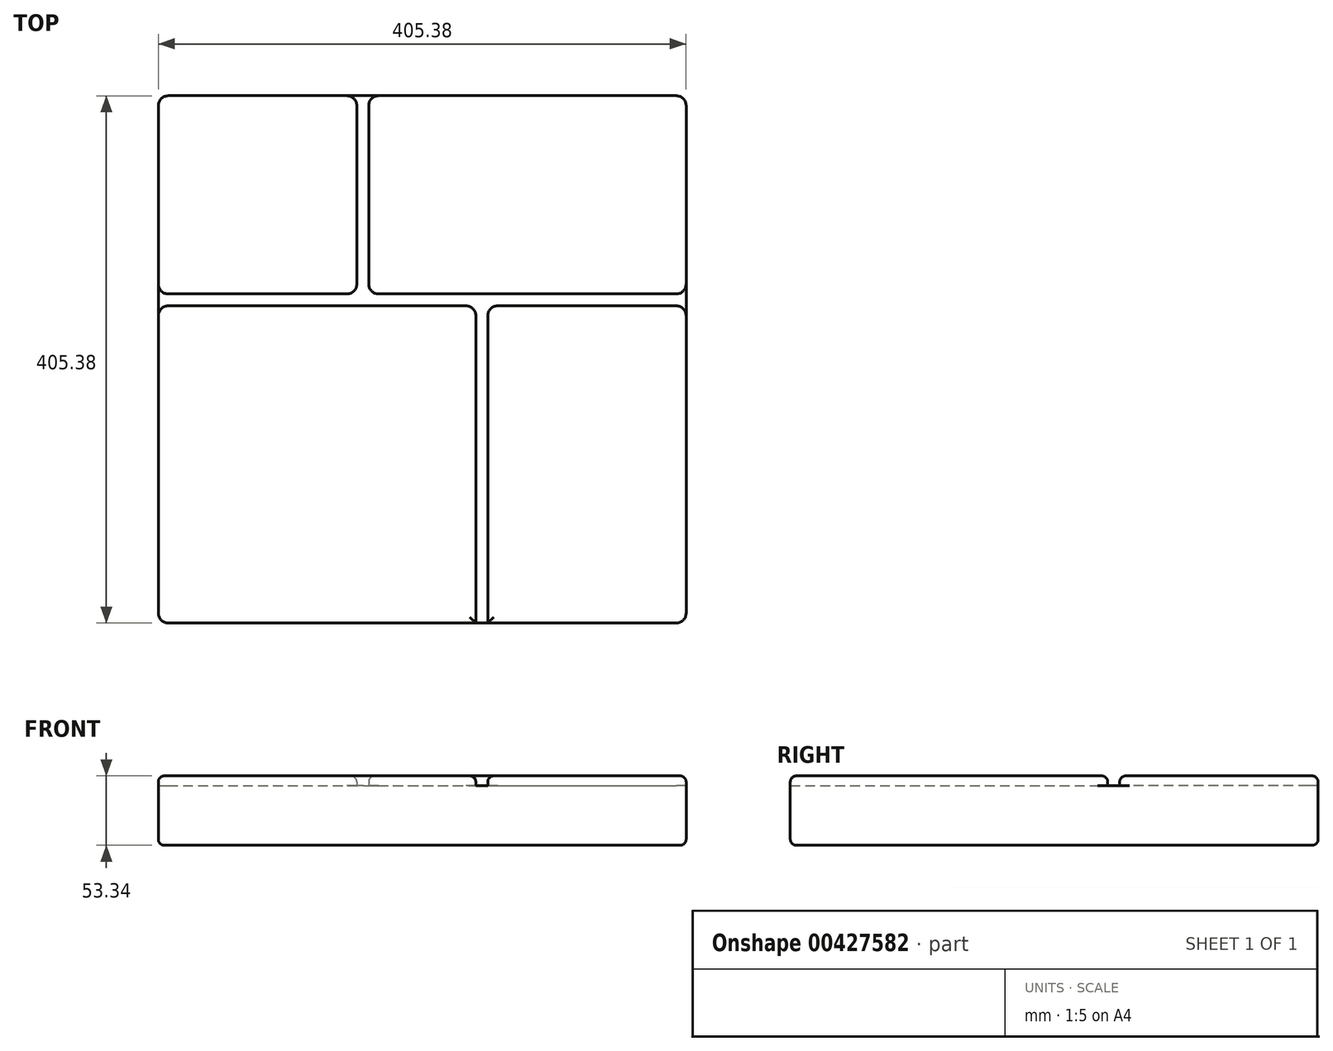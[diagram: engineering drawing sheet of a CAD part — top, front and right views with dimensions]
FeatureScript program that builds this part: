
annotation { "Feature Type Name" : "Feature", "Feature Type Description" : "" }
export const myFeature = defineFeature(function(context is Context, id is Id, definition is map)
    precondition{}
    {
        {
            var Q0;
            Q0=qCreatedBy(makeId("Top.planeOp"),FACE);
            var sketch = newSketch(context, id + "F0", { "sketchPlane" : qUnion([Q0])});
            skLineSegment(sketch, "E0.bottom", {"start": v(202.7, -202.7) * mm, "end": v(-202.7, -202.7) * mm});
            skLineSegment(sketch, "E0.top", {"start": v(202.7, 202.7) * mm, "end": v(-202.7, 202.7) * mm});
            skLineSegment(sketch, "E0.left", {"start": v(202.7, -202.7) * mm, "end": v(202.7, 202.7) * mm});
            skLineSegment(sketch, "E0.right", {"start": v(-202.7, -202.7) * mm, "end": v(-202.7, 202.7) * mm});
            skPoint(sketch, "E0.middle", {"position": v(0, 0) * mm});
            skSolve(sketch);
        }
        {
            var Q0;
            Q0=makeQuery(id+"F0.imprint","IMPRINT",FACE,{"disambiguationData":[TD([[makeQuery(id+"F0.imprint","IMPRINT",EDGE,{"derivedFrom":sQuery(id+"F0.wireOp",EDGE,"E0.bottom")}),-1.0]])]});
            extrude(context, id + "F1", {"entities" : qUnion([Q0]), "depth" : 45.72 * mm});
        }
        {
            var Q0;
            Q0=makeQuery(id+"F1.opExtrude","CAP_FACE",FACE,{"disambiguationData":[OSD([sQuery(id+"F0.wireOp",EDGE,"E0.bottom"),sQuery(id+"F0.wireOp",EDGE,"E0.top"),sQuery(id+"F0.wireOp",EDGE,"E0.left"),sQuery(id+"F0.wireOp",EDGE,"E0.right")])],"isStart":false});
            var sketch = newSketch(context, id + "F2", { "sketchPlane" : qUnion([Q0])});
            skLineSegment(sketch, "E1.bottom", {"start": v(-202.7, -202.7) * mm, "end": v(41.15, -202.7) * mm});
            skLineSegment(sketch, "E1.left", {"start": v(-202.7, -202.7) * mm, "end": v(-202.7, 33.53) * mm});
            skLineSegment(sketch, "E1.right", {"start": v(41.15, -202.7) * mm, "end": v(41.15, 33.53) * mm});
            skLineSegment(sketch, "E2.bottom", {"start": v(-202.7, 202.7) * mm, "end": v(-57.91, 202.7) * mm});
            skLineSegment(sketch, "E2.top", {"start": v(-195.07, 50.3) * mm, "end": v(-57.91, 50.3) * mm});
            skLineSegment(sketch, "E2.left", {"start": v(-202.7, 202.7) * mm, "end": v(-202.7, 57.91) * mm});
            skLineSegment(sketch, "E2.right", {"start": v(-50.3, 195.07) * mm, "end": v(-50.3, 57.91) * mm});
            skLineSegment(sketch, "E3.bottom", {"start": v(-33.53, 202.7) * mm, "end": v(202.7, 202.7) * mm});
            skLineSegment(sketch, "E3.top", {"start": v(-33.53, 50.3) * mm, "end": v(195.07, 50.3) * mm});
            skLineSegment(sketch, "E3.left", {"start": v(-41.15, 195.07) * mm, "end": v(-41.15, 57.91) * mm});
            skLineSegment(sketch, "E3.right", {"start": v(202.7, 202.7) * mm, "end": v(202.7, 57.91) * mm});
            skLineSegment(sketch, "E4.bottom", {"start": v(202.7, -202.7) * mm, "end": v(50.3, -202.7) * mm});
            skLineSegment(sketch, "E4.left", {"start": v(202.7, -202.7) * mm, "end": v(202.7, 33.53) * mm});
            skLineSegment(sketch, "E4.right", {"start": v(50.3, -202.7) * mm, "end": v(50.3, 33.53) * mm});
            skLineSegment(sketch, "E5", {"start": v(-195.07, 41.15) * mm, "end": v(33.53, 41.15) * mm});
            skPoint(sketch, "E6.orphan", {"position": v(41.15, 0) * mm});
            skPoint(sketch, "E7.orphan", {"position": v(50.3, 0) * mm});
            skLineSegment(sketch, "E8.trimOffspring", {"start": v(57.91, 41.15) * mm, "end": v(195.07, 41.15) * mm});
            skPoint(sketch, "E9.visualSharp", {"position": v(-50.3, 50.3) * mm});
            skArc(sketch, "E9.filletArc", {"start": v(-57.91, 50.3) * mm, "mid": v(-52.52, 52.52) * mm, "end": v(-50.3, 57.91) * mm});
            skPoint(sketch, "E10.visualSharp", {"position": v(-41.15, 50.3) * mm});
            skArc(sketch, "E10.filletArc", {"start": v(-41.15, 57.91) * mm, "mid": v(-38.92, 52.52) * mm, "end": v(-33.53, 50.3) * mm});
            skPoint(sketch, "E11.visualSharp", {"position": v(50.3, 41.15) * mm});
            skArc(sketch, "E11.filletArc", {"start": v(57.91, 41.15) * mm, "mid": v(52.52, 38.92) * mm, "end": v(50.3, 33.53) * mm});
            skPoint(sketch, "E12.visualSharp", {"position": v(41.15, 41.15) * mm});
            skArc(sketch, "E12.filletArc", {"start": v(41.15, 33.53) * mm, "mid": v(38.92, 38.92) * mm, "end": v(33.53, 41.15) * mm});
            skPoint(sketch, "E13.visualSharp", {"position": v(-41.15, 202.7) * mm});
            skArc(sketch, "E13.filletArc", {"start": v(-33.53, 202.7) * mm, "mid": v(-38.92, 200.46) * mm, "end": v(-41.15, 195.07) * mm});
            skPoint(sketch, "E14.visualSharp", {"position": v(-50.3, 202.7) * mm});
            skArc(sketch, "E14.filletArc", {"start": v(-50.3, 195.07) * mm, "mid": v(-52.52, 200.46) * mm, "end": v(-57.91, 202.7) * mm});
            skPoint(sketch, "E15.visualSharp", {"position": v(-202.7, 50.3) * mm});
            skArc(sketch, "E15.filletArc", {"start": v(-202.7, 57.91) * mm, "mid": v(-200.46, 52.52) * mm, "end": v(-195.07, 50.3) * mm});
            skPoint(sketch, "E16.visualSharp", {"position": v(-202.7, 41.15) * mm});
            skArc(sketch, "E16.filletArc", {"start": v(-195.07, 41.15) * mm, "mid": v(-200.46, 38.92) * mm, "end": v(-202.7, 33.53) * mm});
            skPoint(sketch, "E17.visualSharp", {"position": v(202.7, 41.15) * mm});
            skArc(sketch, "E17.filletArc", {"start": v(202.7, 33.53) * mm, "mid": v(200.46, 38.92) * mm, "end": v(195.07, 41.15) * mm});
            skPoint(sketch, "E18.visualSharp", {"position": v(202.7, 50.3) * mm});
            skArc(sketch, "E18.filletArc", {"start": v(195.07, 50.3) * mm, "mid": v(200.46, 52.52) * mm, "end": v(202.7, 57.91) * mm});
            skSolve(sketch);
        }
        {
            var Q0;
            Q0=makeQuery(id+"F2.imprint","IMPRINT",FACE,{"disambiguationData":[TD([[makeQuery(id+"F2.imprint","IMPRINT",EDGE,{"derivedFrom":sQuery(id+"F2.wireOp",EDGE,"E2.bottom")}),1.0]])]});
            var Q1;
            Q1=makeQuery(id+"F2.imprint","IMPRINT",FACE,{"disambiguationData":[TD([[makeQuery(id+"F2.imprint","IMPRINT",EDGE,{"derivedFrom":sQuery(id+"F2.wireOp",EDGE,"E3.bottom")}),1.0]])]});
            var Q2;
            Q2=makeQuery(id+"F2.imprint","IMPRINT",FACE,{"disambiguationData":[TD([[makeQuery(id+"F2.imprint","IMPRINT",EDGE,{"derivedFrom":sQuery(id+"F2.wireOp",EDGE,"E4.bottom")}),-1.0]])]});
            var Q3;
            Q3=makeQuery(id+"F2.imprint","IMPRINT",FACE,{"disambiguationData":[TD([[makeQuery(id+"F2.imprint","IMPRINT",EDGE,{"derivedFrom":sQuery(id+"F2.wireOp",EDGE,"E1.bottom")}),-1.0]])]});
            extrude(context, id + "F3", {"entities" : qUnion([Q0, Q1, Q2, Q3]), "operationType" : NewBodyOperationType.ADD, "depth" : 7.62 * mm});
        }
        {
            var Q0;
            Q0=makeQuery(id+"F3.boolean.opBoolean","MERGE",EDGE,{"derivedFrom":[makeQuery(id+"F1.opExtrude","SWEPT_EDGE",EDGE,{"disambiguationData":[OSD([sQuery(id+"F0.wireOp",EDGE,"E0.top"),sQuery(id+"F0.wireOp",EDGE,"E0.right")])]}),makeQuery(id+"F3.opExtrude","SWEPT_EDGE",EDGE,{"disambiguationData":[OSD([sQuery(id+"F2.wireOp",EDGE,"E2.bottom"),sQuery(id+"F2.wireOp",EDGE,"E2.left")])]})]});
            var Q1;
            Q1=makeQuery(id+"F3.boolean.opBoolean","MERGE",EDGE,{"derivedFrom":[makeQuery(id+"F1.opExtrude","SWEPT_EDGE",EDGE,{"disambiguationData":[OSD([sQuery(id+"F0.wireOp",EDGE,"E0.top"),sQuery(id+"F0.wireOp",EDGE,"E0.left")])]}),makeQuery(id+"F3.opExtrude","SWEPT_EDGE",EDGE,{"disambiguationData":[OSD([sQuery(id+"F2.wireOp",EDGE,"E3.bottom"),sQuery(id+"F2.wireOp",EDGE,"E3.right")])]})]});
            var Q2;
            Q2=makeQuery(id+"F3.boolean.opBoolean","MERGE",EDGE,{"derivedFrom":[makeQuery(id+"F1.opExtrude","SWEPT_EDGE",EDGE,{"disambiguationData":[OSD([sQuery(id+"F0.wireOp",EDGE,"E0.bottom"),sQuery(id+"F0.wireOp",EDGE,"E0.left")])]}),makeQuery(id+"F3.opExtrude","SWEPT_EDGE",EDGE,{"disambiguationData":[OSD([sQuery(id+"F2.wireOp",EDGE,"E4.bottom"),sQuery(id+"F2.wireOp",EDGE,"E4.left")])]})]});
            var Q3;
            Q3=makeQuery(id+"F3.boolean.opBoolean","MERGE",EDGE,{"derivedFrom":[makeQuery(id+"F1.opExtrude","SWEPT_EDGE",EDGE,{"disambiguationData":[OSD([sQuery(id+"F0.wireOp",EDGE,"E0.bottom"),sQuery(id+"F0.wireOp",EDGE,"E0.right")])]}),makeQuery(id+"F3.opExtrude","SWEPT_EDGE",EDGE,{"disambiguationData":[OSD([sQuery(id+"F2.wireOp",EDGE,"E1.bottom"),sQuery(id+"F2.wireOp",EDGE,"E1.left")])]})]});
            fillet(context, id + "F4", {"entities" : qUnion([Q0, Q1, Q2, Q3]), "radius" : 7.62 * mm, "tangentPropagation" : true, "allowEdgeOverflow" : false});
        }
        {
            var Q0;
            Q0=makeQuery(id+"F3.opExtrude","CAP_FACE",FACE,{"disambiguationData":[OSD([sQuery(id+"F2.wireOp",EDGE,"E3.bottom"),sQuery(id+"F2.wireOp",EDGE,"E3.top"),sQuery(id+"F2.wireOp",EDGE,"E3.left"),sQuery(id+"F2.wireOp",EDGE,"E3.right"),sQuery(id+"F2.wireOp",EDGE,"E10.filletArc"),sQuery(id+"F2.wireOp",EDGE,"E13.filletArc"),sQuery(id+"F2.wireOp",EDGE,"E18.filletArc")])],"isStart":false});
            var Q1;
            Q1=makeQuery(id+"F3.opExtrude","CAP_FACE",FACE,{"disambiguationData":[OSD([sQuery(id+"F2.wireOp",EDGE,"E4.bottom"),sQuery(id+"F2.wireOp",EDGE,"E4.left"),sQuery(id+"F2.wireOp",EDGE,"E4.right"),sQuery(id+"F2.wireOp",EDGE,"E8.trimOffspring"),sQuery(id+"F2.wireOp",EDGE,"E11.filletArc"),sQuery(id+"F2.wireOp",EDGE,"E17.filletArc")])],"isStart":false});
            var Q2;
            Q2=makeQuery(id+"F3.opExtrude","CAP_FACE",FACE,{"disambiguationData":[OSD([sQuery(id+"F2.wireOp",EDGE,"E1.bottom"),sQuery(id+"F2.wireOp",EDGE,"E1.left"),sQuery(id+"F2.wireOp",EDGE,"E1.right"),sQuery(id+"F2.wireOp",EDGE,"E5"),sQuery(id+"F2.wireOp",EDGE,"E12.filletArc"),sQuery(id+"F2.wireOp",EDGE,"E16.filletArc")])],"isStart":false});
            var Q3;
            Q3=makeQuery(id+"F3.opExtrude","CAP_FACE",FACE,{"disambiguationData":[OSD([sQuery(id+"F2.wireOp",EDGE,"E2.bottom"),sQuery(id+"F2.wireOp",EDGE,"E2.top"),sQuery(id+"F2.wireOp",EDGE,"E2.left"),sQuery(id+"F2.wireOp",EDGE,"E2.right"),sQuery(id+"F2.wireOp",EDGE,"E9.filletArc"),sQuery(id+"F2.wireOp",EDGE,"E14.filletArc"),sQuery(id+"F2.wireOp",EDGE,"E15.filletArc")])],"isStart":false});
            var Q4;
            Q4=makeQuery(id+"F1.opExtrude","CAP_FACE",FACE,{"disambiguationData":[OSD([sQuery(id+"F0.wireOp",EDGE,"E0.bottom"),sQuery(id+"F0.wireOp",EDGE,"E0.top"),sQuery(id+"F0.wireOp",EDGE,"E0.left"),sQuery(id+"F0.wireOp",EDGE,"E0.right")])],"isStart":true});
            fillet(context, id + "F5", {"entities" : qUnion([Q0, Q1, Q2, Q3, Q4]), "radius" : 4.57 * mm, "tangentPropagation" : true, "allowEdgeOverflow" : false});
        }
    });
